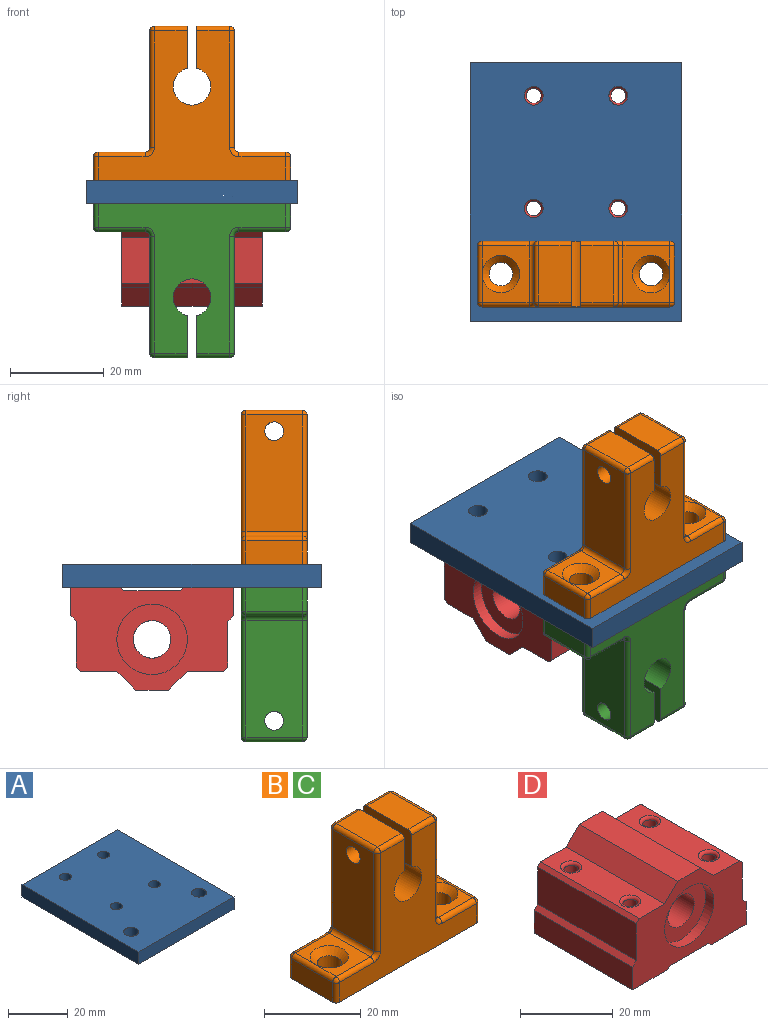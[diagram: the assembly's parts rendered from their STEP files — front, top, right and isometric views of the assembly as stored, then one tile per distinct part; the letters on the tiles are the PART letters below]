
ASSEMBLY  parts=4 mates=9
PART A: 12 faces, bbox 45x55x5 mm
  f0: plane 55x45mm, normal (0,0,1), area 2385.5mm2, adj f2,f3,f4,f5,f6,f7,f8,f9
  f1: plane 55x45mm, normal (0,0,-1), area 2385.5mm2, adj f2,f3,f4,f5,f6,f7,f8,f9
  f2: plane 45x5mm, normal (0,-1,0), area 225mm2, adj f0,f1,f3,f5
  f3: plane 55x5mm, normal (1,0,0), area 275mm2, adj f0,f1,f2,f4
  f4: plane 45x5mm, normal (0,1,0), area 225mm2, adj f0,f1,f3,f5
  f5: plane 55x5mm, normal (-1,0,0), area 275mm2, adj f0,f1,f2,f4
  f6: cylinder r=2mm len=5mm, axis (0,0,1), area 62.8mm2, adj f0,f1
  f7: cylinder r=2mm len=5mm, axis (0,0,1), area 62.8mm2, adj f0,f1
  f8: cylinder r=2.5mm len=5mm, axis (0,0,1), area 78.5mm2, adj f0,f1
  f9: cylinder r=2mm len=5mm, axis (0,0,1), area 62.8mm2, adj f0,f1
  f10: cylinder r=2mm len=5mm, axis (0,0,1), area 62.8mm2, adj f0,f1
  f11: cylinder r=2.5mm len=5mm, axis (0,0,1), area 78.5mm2, adj f0,f1
PART B: 54 faces, bbox 42x14x32.8 mm
  f0: plane 12x7mm, normal (0,0,1), area 84mm2, adj f14,f39,f47,f48
  f1: plane 12x10mm, normal (0,0,1), area 69.7mm2, adj f18,f41,f42,f49,f50
  f2: plane 12x10mm, normal (0,0,1), area 69.7mm2, adj f19,f24,f25,f32,f33
  f3: plane 42x14mm, normal (0,0,-1), area 547.9mm2, adj f4,f5,f6,f7,f8,f9,f20,f26
  f4: plane 40x31.8mm, normal (0,-1,0), area 564.6mm2, adj f3,f13,f14,f15,f20,f22,f23,f24
  f5: plane 12x5mm, normal (1,0,0), area 60mm2, adj f3,f37,f40,f41
  f6: plane 40x31.8mm, normal (0,1,0), area 564.6mm2, adj f3,f13,f14,f15,f26,f30,f33,f35
  f7: plane 12x5mm, normal (-1,0,0), area 60mm2, adj f3,f20,f25,f26
  f8: cylinder r=2.5mm len=5mm, axis (0,0,1), area 70.7mm2, adj f3,f18
  f9: cylinder r=2.5mm len=5mm, axis (0,0,1), area 70.7mm2, adj f3,f19
  f10: plane 24.8x12mm, normal (1,0,0), area 285mm2, adj f17,f43,f47,f50,f53
  f11: plane 24.8x12mm, normal (-1,0,0), area 285mm2, adj f16,f23,f31,f32,f36
  f12: plane 12x7mm, normal (0,0,1), area 84mm2, adj f15,f22,f30,f31
  f13: cylinder r=4mm len=14mm, axis (0,-1,0), area 323.6mm2, adj f4,f6,f14,f15
  f14: plane 14x8.93mm, normal (-1,0,0), area 112mm2, adj f0,f4,f6,f13,f17,f39,f48
  f15: plane 14x8.93mm, normal (1,0,0), area 112mm2, adj f4,f6,f12,f13,f16,f22,f30
  f16: cylinder r=2mm len=8mm, axis (1,0,0), area 100.5mm2, adj f11,f15
  f17: cylinder r=2mm len=8mm, axis (1,0,0), area 100.5mm2, adj f10,f14
  f18: cone r=4mm half-angle=45deg, axis (0,0,1), area 43.3mm2, adj f1,f8
  f19: cone r=2.5mm half-angle=45deg, axis (0,0,1), area 43.3mm2, adj f2,f9
  f20: cylinder r=1mm len=5mm, axis (0,0,1), area 7.9mm2, adj f3,f4,f7,f21
  f21: sphere r=1mm, area 1.6mm2, adj f20,f24,f25
  f22: cylinder r=1mm len=7mm, axis (-1,0,0), area 11mm2, adj f4,f12,f15,f27
  f23: cylinder r=1mm len=24.8mm, axis (0,0,1), area 39mm2, adj f4,f11,f27,f28
  f24: cylinder r=1mm len=10mm, axis (-1,0,0), area 15.7mm2, adj f2,f4,f21,f28
  f25: cylinder r=1mm len=12mm, axis (0,1,0), area 18.8mm2, adj f2,f7,f21,f29
  f26: cylinder r=1mm len=5mm, axis (0,0,-1), area 7.9mm2, adj f3,f6,f7,f29
  f27: sphere r=1mm, area 1.6mm2, adj f22,f23,f31
  f28: torus R=2mm, axis (0,-1,0), area 3.4mm2, adj f4,f23,f24,f32
  f29: sphere r=1mm, area 1.6mm2, adj f25,f26,f33
  f30: cylinder r=1mm len=7mm, axis (1,0,0), area 11mm2, adj f6,f12,f15,f34
  f31: cylinder r=1mm len=12mm, axis (0,1,0), area 18.8mm2, adj f11,f12,f27,f34
  f32: cylinder r=1mm len=12mm, axis (0,-1,0), area 18.8mm2, adj f2,f11,f28,f35
  f33: cylinder r=1mm len=10mm, axis (1,0,0), area 15.7mm2, adj f2,f6,f29,f35
  f34: sphere r=1mm, area 1.6mm2, adj f30,f31,f36
  f35: torus R=2mm, axis (0,-1,0), area 3.4mm2, adj f6,f32,f33,f36
  f36: cylinder r=1mm len=24.8mm, axis (0,0,-1), area 39mm2, adj f6,f11,f34,f35
  f37: cylinder r=1mm len=5mm, axis (0,0,-1), area 7.9mm2, adj f3,f4,f5,f38
  f38: sphere r=1mm, area 1.6mm2, adj f37,f41,f42
  f39: cylinder r=1mm len=7mm, axis (-1,0,0), area 11mm2, adj f0,f4,f14,f44
  f40: cylinder r=1mm len=5mm, axis (0,0,1), area 7.9mm2, adj f3,f5,f6,f45
  f41: cylinder r=1mm len=12mm, axis (0,-1,0), area 18.8mm2, adj f1,f5,f38,f45
  f42: cylinder r=1mm len=10mm, axis (-1,0,0), area 15.7mm2, adj f1,f4,f38,f46
  f43: cylinder r=1mm len=24.8mm, axis (0,0,-1), area 39mm2, adj f4,f10,f44,f46
  f44: sphere r=1mm, area 1.6mm2, adj f39,f43,f47
  f45: sphere r=1mm, area 1.6mm2, adj f40,f41,f49
  f46: torus R=2mm, axis (0,-1,0), area 3.4mm2, adj f4,f42,f43,f50
  f47: cylinder r=1mm len=12mm, axis (0,-1,0), area 18.8mm2, adj f0,f10,f44,f51
  f48: cylinder r=1mm len=7mm, axis (1,0,0), area 11mm2, adj f0,f6,f14,f51
  f49: cylinder r=1mm len=10mm, axis (1,0,0), area 15.7mm2, adj f1,f6,f45,f52
  f50: cylinder r=1mm len=12mm, axis (0,1,0), area 18.8mm2, adj f1,f10,f46,f52
  f51: sphere r=1mm, area 1.6mm2, adj f47,f48,f53
  f52: torus R=2mm, axis (0,-1,0), area 3.4mm2, adj f6,f49,f50,f53
  f53: cylinder r=1mm len=24.8mm, axis (0,0,1), area 39mm2, adj f6,f10,f51,f52
PART C: same geometry as B
PART D: 37 faces, bbox 34.6x30x21.8 mm
  f0: plane 34.6x21.8mm, normal (0,1,0), area 448.1mm2, adj f1,f2,f3,f4,f5,f6,f7,f8
  f1: plane 30x7.74mm, normal (0,0,1), area 199.4mm2, adj f0,f16,f17,f32,f33,f36
  f2: plane 30x9.76mm, normal (-1,0,0), area 292.8mm2, adj f0,f3,f17,f36
  f3: plane 30x1.16mm, normal (-0.71,0,0.71), area 49.2mm2, adj f0,f2,f4,f17
  f4: plane 30x5.98mm, normal (-1,0,0), area 179.4mm2, adj f0,f3,f5,f17
  f5: plane 30x10.65mm, normal (0,0,-1), area 277.5mm2, adj f0,f4,f6,f17,f27,f29
  f6: plane 30x0.65mm, normal (0.71,0,-0.71), area 27.6mm2, adj f0,f5,f7,f17
  f7: plane 30x12mm, normal (0,0,-1), area 360mm2, adj f0,f6,f8,f17
  f8: plane 30x0.65mm, normal (-0.71,0,-0.71), area 27.6mm2, adj f0,f7,f9,f17
  f9: plane 30x10.65mm, normal (0,0,-1), area 277.5mm2, adj f0,f8,f10,f17,f28,f30
  f10: plane 30x5.98mm, normal (1,0,0), area 179.4mm2, adj f0,f9,f11,f17
  f11: plane 30x1.16mm, normal (0.71,0,0.71), area 49.2mm2, adj f0,f10,f12,f17
  f12: plane 30x9.76mm, normal (1,0,0), area 292.8mm2, adj f0,f11,f17,f35
  f13: plane 30x7.74mm, normal (0,0,1), area 199.4mm2, adj f0,f14,f17,f31,f34,f35
  f14: plane 30x4mm, normal (0.71,0,0.71), area 169.7mm2, adj f0,f13,f15,f17
  f15: plane 30x7mm, normal (0,0,1), area 210mm2, adj f0,f14,f16,f17
  f16: plane 30x4mm, normal (-0.71,0,0.71), area 169.7mm2, adj f0,f1,f15,f17
  f17: plane 34.6x21.8mm, normal (0,-1,0), area 448.1mm2, adj f1,f2,f3,f4,f5,f6,f7,f8
  f18: cylinder r=7.5mm len=15mm, axis (0,-1,0), area 117.8mm2, adj f17,f19
  f19: plane 15x15mm, normal (0,-1,0), area 126.4mm2, adj f18,f22
  f20: cylinder r=7.5mm len=15mm, axis (0,1,0), area 117.8mm2, adj f0,f21
  f21: plane 15x15mm, normal (0,1,0), area 126.4mm2, adj f20,f22
  f22: cylinder r=4mm len=25mm, axis (0,-1,0), area 628.3mm2, adj f19,f21
  f23: cylinder r=1.58mm len=16.1mm, axis (0,0,-1), area 160.3mm2, adj f29,f33
  f24: cylinder r=1.58mm len=16.1mm, axis (0,0,-1), area 160.3mm2, adj f27,f32
  f25: cylinder r=1.58mm len=16.1mm, axis (0,0,-1), area 160.3mm2, adj f28,f31
  f26: cylinder r=1.58mm len=16.1mm, axis (0,0,-1), area 160.3mm2, adj f30,f34
  f27: torus R=2.58mm, axis (0,0,1), area 19.2mm2, adj f5,f24
  f28: torus R=2.58mm, axis (0,0,1), area 19.2mm2, adj f9,f25
  f29: torus R=2.58mm, axis (0,0,1), area 19.2mm2, adj f5,f23
  f30: torus R=2.58mm, axis (0,0,1), area 19.2mm2, adj f9,f26
  f31: torus R=2.29mm, axis (0,0,-1), area 12.7mm2, adj f13,f25
  f32: torus R=2.29mm, axis (0,0,-1), area 12.7mm2, adj f1,f24
  f33: torus R=2.29mm, axis (0,0,-1), area 12.7mm2, adj f1,f23
  f34: torus R=2.29mm, axis (0,0,-1), area 12.7mm2, adj f13,f26
  f35: plane 30x0.9mm, normal (0.71,0,0.71), area 38.2mm2, adj f0,f12,f13,f17
  f36: plane 30x0.9mm, normal (-0.71,0,0.71), area 38.2mm2, adj f0,f1,f2,f17
PLACE A t=(14.11,-23.12,-10.48)mm
PLACE B t=(14.11,-40.62,-5.48)mm
PLACE C rot(axis=(1,0,0),180deg) t=(14.11,-40.62,-10.48)mm
PLACE D rot(axis=(0.71,-0.71,0),180deg) t=(14.11,-14.62,-19.71)mm
MATE planar B.f3 <-> A.f0  axis (0,0,-1) through (14.11,-40.62,-5.48)mm
MATE parallel C.f6 <-> B.f4  axis (0,-1,0) through (14.11,-47.62,-22.8)mm
MATE cylindrical D.f26 <-> A.f7  axis (0,0,1) through (23.11,-26.62,-19.53)mm
MATE parallel D.f17 <-> A.f3  axis (1,0,0) through (29.11,-14.62,-19.55)mm
MATE cylindrical B.f9 <-> A.f8  axis (0,0,1) through (-1.89,-40.62,-3.23)mm
MATE planar D.f5 <-> A.f1  axis (0,0,1) through (14.11,-2.64,-10.48)mm
MATE parallel B.f4 <-> A.f2  axis (0,-1,0) through (14.11,-47.62,6.84)mm
MATE cylindrical C.f9 <-> A.f8  axis (0,0,-1) through (-1.89,-40.62,-12.73)mm
MATE planar C.f3 <-> A.f1  axis (0,0,1) through (14.11,-40.62,-10.48)mm
